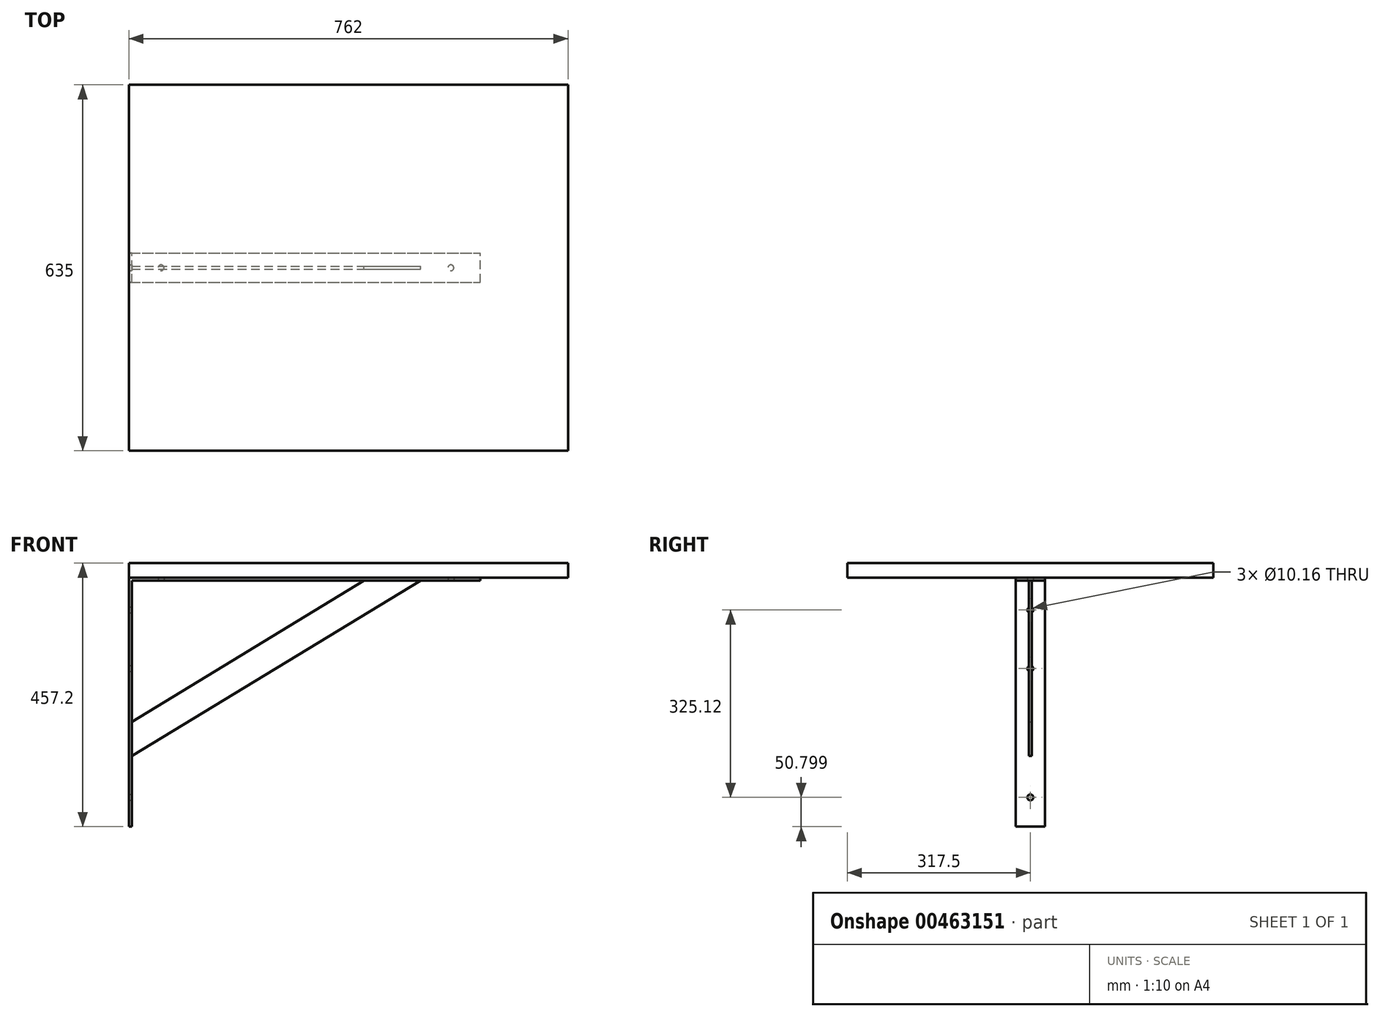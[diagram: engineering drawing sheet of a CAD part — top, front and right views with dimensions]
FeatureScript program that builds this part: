
annotation { "Feature Type Name" : "Feature", "Feature Type Description" : "" }
export const myFeature = defineFeature(function(context is Context, id is Id, definition is map)
    precondition{}
    {
        {
            var Q0;
            Q0=qCreatedBy(makeId("Front.planeOp"),FACE);
            var sketch = newSketch(context, id + "F0", { "sketchPlane" : qUnion([Q0])});
            skLineSegment(sketch, "E0", {"start": v(-29.59, 365.04) * mm, "end": v(-29.59, -371.56) * mm});
            skLineSegment(sketch, "E1", {"start": v(-29.59, 365.04) * mm, "end": v(732.41, 365.04) * mm});
            skLineSegment(sketch, "E2", {"start": v(732.41, 365.04) * mm, "end": v(732.41, 390.44) * mm});
            skLineSegment(sketch, "E3", {"start": v(732.41, 390.44) * mm, "end": v(-29.59, 390.44) * mm});
            skLineSegment(sketch, "E4", {"start": v(-29.59, 390.44) * mm, "end": v(-29.59, 365.04) * mm});
            skLineSegment(sketch, "E5.0", {"start": v(-24.5, 359.96) * mm, "end": v(580.01, 359.96) * mm});
            skLineSegment(sketch, "E6.0", {"start": v(-24.5, 359.96) * mm, "end": v(-24.5, -66.76) * mm});
            skLineSegment(sketch, "E7", {"start": v(-24.5, -66.76) * mm, "end": v(-29.59, -66.76) * mm});
            skLineSegment(sketch, "E8", {"start": v(580.01, 365.04) * mm, "end": v(580.01, 359.96) * mm});
            skLineSegment(sketch, "E9.0", {"start": v(427.61, 365.04) * mm, "end": v(427.61, 359.96) * mm});
            skLineSegment(sketch, "E10.0", {"start": v(-24.5, 85.64) * mm, "end": v(-29.59, 85.64) * mm});
            skLineSegment(sketch, "E11", {"start": v(-24.5, 85.64) * mm, "end": v(427.61, 359.96) * mm});
            skLineSegment(sketch, "E12.0", {"start": v(-11.33, 63.92) * mm, "end": v(440.79, 338.24) * mm});
            skLineSegment(sketch, "E13", {"start": v(440.79, 338.24) * mm, "end": v(476.58, 359.96) * mm});
            skLineSegment(sketch, "E14", {"start": v(-11.33, 63.92) * mm, "end": v(-24.5, 55.93) * mm});
            skLineSegment(sketch, "E15.trimOffspring", {"start": v(-24.5, 115.35) * mm, "end": v(378.65, 359.96) * mm});
            skSolve(sketch);
        }
        {
            var Q0;
            {var subQ1=sQuery(id+"F0.wireOp",EDGE,"E9.0");Q0=makeQuery(id+"F0.imprint","IMPRINT",FACE,{"disambiguationData":[TD([[makeQuery(id+"F0.imprint","IMPRINT",EDGE,{"derivedFrom":subQ1}),-1.0]])]});}
            var Q1;
            {var subQ0=sQuery(id+"F0.wireOp",EDGE,"E8");Q1=makeQuery(id+"F0.imprint","IMPRINT",FACE,{"disambiguationData":[TD([[makeQuery(id+"F0.imprint","IMPRINT",EDGE,{"derivedFrom":subQ0}),-1.0]])]});}
            var Q2;
            {var subQ0=sQuery(id+"F0.wireOp",EDGE,"E7");Q2=makeQuery(id+"F0.imprint","IMPRINT",FACE,{"disambiguationData":[TD([[makeQuery(id+"F0.imprint","IMPRINT",EDGE,{"derivedFrom":subQ0}),-1.0]])]});}
            extrude(context, id + "F1", {"entities" : qUnion([Q0, Q1, Q2]), "endBound" : BoundingType.SYMMETRIC, "depth" : 50.8 * mm});
        }
        {
            var Q0;
            {var subQ0=sQuery(id+"F0.wireOp",EDGE,"E11");Q0=makeQuery(id+"F0.imprint","IMPRINT",FACE,{"disambiguationData":[TD([[makeQuery(id+"F0.imprint","IMPRINT",EDGE,{"derivedFrom":subQ0}),1.0]])]});}
            var Q1;
            {var subQ0=sQuery(id+"F0.wireOp",EDGE,"E11");Q1=makeQuery(id+"F0.imprint","IMPRINT",FACE,{"disambiguationData":[TD([[makeQuery(id+"F0.imprint","IMPRINT",EDGE,{"derivedFrom":subQ0}),-1.0]])]});}
            extrude(context, id + "F2", {"entities" : qUnion([Q0, Q1]), "operationType" : NewBodyOperationType.ADD, "endBound" : BoundingType.SYMMETRIC, "depth" : 5.08 * mm});
        }
        {
            var Q0;
            {var subQ0=sQuery(id+"F0.wireOp",EDGE,"E2");Q0=makeQuery(id+"F0.imprint","IMPRINT",FACE,{"disambiguationData":[TD([[makeQuery(id+"F0.imprint","IMPRINT",EDGE,{"derivedFrom":subQ0}),1.0]])]});}
            extrude(context, id + "F3", {"entities" : qUnion([Q0]), "endBound" : BoundingType.SYMMETRIC, "depth" : 635 * mm});
        }
        {
            var Q0;
            Q0=makeQuery(id+"F1.opExtrude","SWEPT_FACE",FACE,{"disambiguationData":[OSD([sQuery(id+"F0.wireOp",EDGE,"E6.0")])]});
            var sketch = newSketch(context, id + "F4", { "sketchPlane" : qUnion([Q0])});
            skCircle(sketch, "E16", {"center": v(0, 309.16) * mm, "radius": 5.08 * mm});
            skPoint(sketch, "E16.centerSnap0", {"position": v(0, 359.96) * mm});
            skCircle(sketch, "E17", {"center": v(0, 207.56) * mm, "radius": 5.08 * mm});
            skLineSegment(sketch, "E18.0", {"start": v(-25.4, 359.96) * mm, "end": v(25.4, 359.96) * mm});
            skLineSegment(sketch, "E19.0", {"start": v(-25.4, -66.76) * mm, "end": v(25.4, -66.76) * mm});
            skCircle(sketch, "E20", {"center": v(0, -15.96) * mm, "radius": 5.08 * mm});
            skSolve(sketch);
        }
        {
            var Q0;
            Q0=makeQuery(id+"F1.opExtrude","SWEPT_FACE",FACE,{"disambiguationData":[OSD([sQuery(id+"F0.wireOp",EDGE,"E5.0")])]});
            var sketch = newSketch(context, id + "F5", { "sketchPlane" : qUnion([Q0])});
            skCircle(sketch, "E21", {"center": v(529.21, 0) * mm, "radius": 5.08 * mm});
            skCircle(sketch, "E22", {"center": v(26.3, 0) * mm, "radius": 5.08 * mm});
            skLineSegment(sketch, "E23.0", {"start": v(-24.5, 25.4) * mm, "end": v(-24.5, -25.4) * mm});
            skLineSegment(sketch, "E24.0", {"start": v(580.01, 25.4) * mm, "end": v(580.01, -25.4) * mm});
            skSolve(sketch);
        }
        {
            var Q0;
            Q0=makeQuery(id+"F4.imprint","IMPRINT",FACE,{"disambiguationData":[TD([[makeQuery(id+"F4.imprint","IMPRINT",EDGE,{"derivedFrom":sQuery(id+"F4.wireOp",EDGE,"E16")}),1.0]])]});
            var Q1;
            Q1=makeQuery(id+"F4.imprint","IMPRINT",FACE,{"disambiguationData":[TD([[makeQuery(id+"F4.imprint","IMPRINT",EDGE,{"derivedFrom":sQuery(id+"F4.wireOp",EDGE,"E20")}),1.0]])]});
            var Q2;
            Q2=makeQuery(id+"F4.imprint","IMPRINT",FACE,{"disambiguationData":[TD([[makeQuery(id+"F4.imprint","IMPRINT",EDGE,{"derivedFrom":sQuery(id+"F4.wireOp",EDGE,"E17")}),1.0]])]});
            extrude(context, id + "F6", {"entities" : qUnion([Q0, Q1, Q2]), "operationType" : NewBodyOperationType.REMOVE, "oppositeDirection" : true, "depth" : 5.08 * mm});
        }
        {
            var Q0;
            Q0=makeQuery(id+"F5.imprint","IMPRINT",FACE,{"disambiguationData":[TD([[makeQuery(id+"F5.imprint","IMPRINT",EDGE,{"derivedFrom":sQuery(id+"F5.wireOp",EDGE,"E22")}),1.0]])]});
            var Q1;
            Q1=makeQuery(id+"F5.imprint","IMPRINT",FACE,{"disambiguationData":[TD([[makeQuery(id+"F5.imprint","IMPRINT",EDGE,{"derivedFrom":sQuery(id+"F5.wireOp",EDGE,"E21")}),1.0]])]});
            extrude(context, id + "F7", {"entities" : qUnion([Q0, Q1]), "operationType" : NewBodyOperationType.REMOVE, "oppositeDirection" : true, "depth" : 5.08 * mm});
        }
    });
